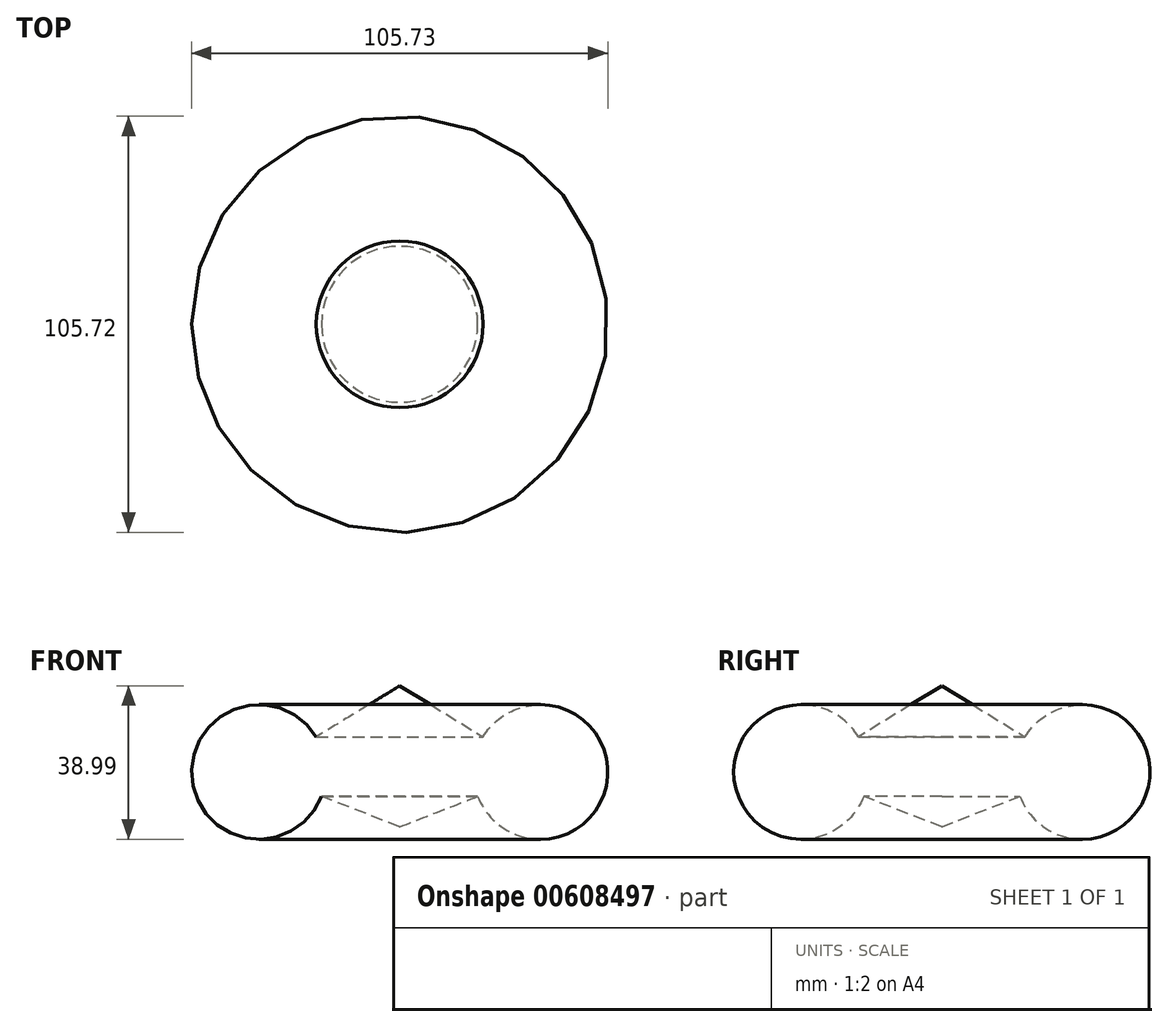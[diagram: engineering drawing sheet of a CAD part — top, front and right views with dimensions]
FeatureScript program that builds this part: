
annotation { "Feature Type Name" : "Feature", "Feature Type Description" : "" }
export const myFeature = defineFeature(function(context is Context, id is Id, definition is map)
    precondition{}
    {
        {
            var Q0;
            Q0=qCreatedBy(makeId("Front.planeOp"),FACE);
            var sketch = newSketch(context, id + "F0", { "sketchPlane" : qUnion([Q0])});
            skCircle(sketch, "E0", {"center": v(-57.97, 18.83) * mm, "radius": 17.1 * mm});
            skLineSegment(sketch, "E1", {"start": v(-57.97, 18.83) * mm, "end": v(-22.2, 40.7) * mm});
            skLineSegment(sketch, "E2", {"start": v(-57.97, 18.83) * mm, "end": v(-22.2, 4.9) * mm});
            skLineSegment(sketch, "E3", {"start": v(-22.2, 4.9) * mm, "end": v(-22.2, 40.7) * mm});
            skSolve(sketch);
        }
        {
            var Q0;
            {var subQ5=sQuery(id+"F0.wireOp",EDGE,"E3");Q0=makeQuery(id+"F0.imprint","IMPRINT",FACE,{"disambiguationData":[TD([[makeQuery(id+"F0.imprint","IMPRINT",EDGE,{"derivedFrom":subQ5}),1.0]])]});}
            var Q1;
            {var subQ0=sQuery(id+"F0.wireOp",EDGE,"E1");var subQ1=sQuery(id+"F0.wireOp",EDGE,"E0");var subQ2=makeQuery(id+"F0.imprint","INTERSECT",VERTEX,{"derivedFrom":[subQ1,subQ0]});Q1=makeQuery(id+"F0.imprint","IMPRINT",FACE,{"disambiguationData":[TD([[makeQuery(id+"F0.imprint","IMPRINT",EDGE,{"disambiguationData":[TD([[subQ2,1.0]])],"derivedFrom":subQ1}),1.0]])]});}
            var Q2;
            {var subQ0=sQuery(id+"F0.wireOp",EDGE,"E1");var subQ1=sQuery(id+"F0.wireOp",EDGE,"E0");var subQ2=makeQuery(id+"F0.imprint","INTERSECT",VERTEX,{"derivedFrom":[subQ1,subQ0]});Q2=makeQuery(id+"F0.imprint","IMPRINT",FACE,{"disambiguationData":[TD([[makeQuery(id+"F0.imprint","IMPRINT",EDGE,{"disambiguationData":[TD([[subQ2,-1.0]])],"derivedFrom":subQ1}),1.0]])]});}
            var Q3;
            Q3=sQuery(id+"F0.wireOp",EDGE,"E3");
            revolve(context, id + "F1", {"entities" : qUnion([Q0, Q1, Q2]), "axis" : qUnion([Q3]), "revolveType" : RevolveType.FULL});
        }
    });
